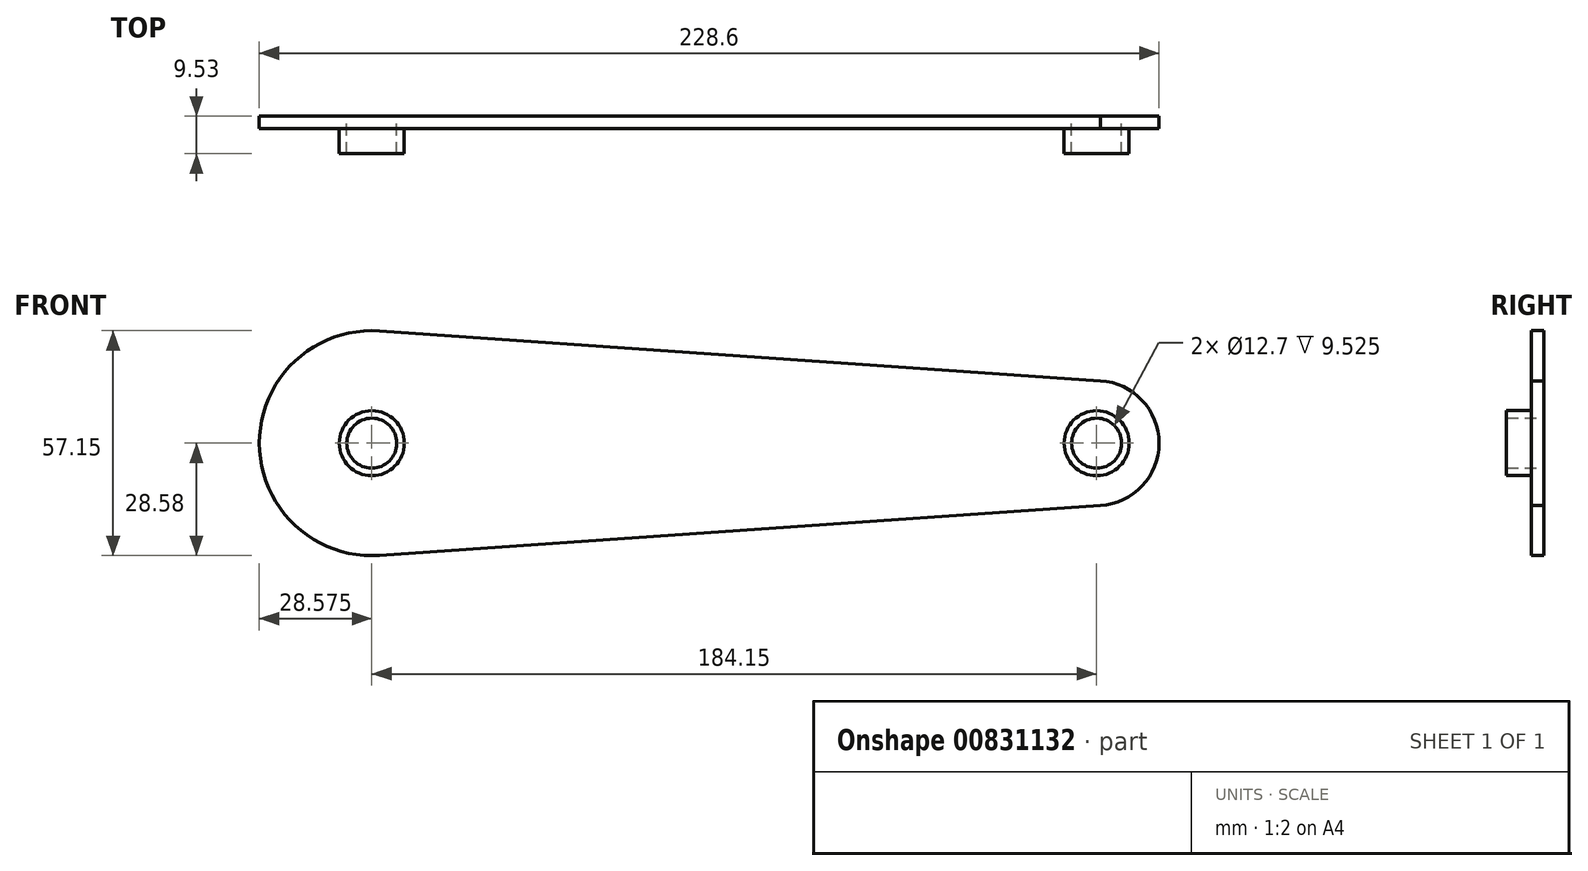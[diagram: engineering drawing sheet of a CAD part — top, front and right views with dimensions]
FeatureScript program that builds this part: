
annotation { "Feature Type Name" : "Feature", "Feature Type Description" : "" }
export const myFeature = defineFeature(function(context is Context, id is Id, definition is map)
    precondition{}
    {
        {
            var Q0;
            Q0=qCreatedBy(makeId("Front.planeOp"),FACE);
            var sketch = newSketch(context, id + "F0", { "sketchPlane" : qUnion([Q0])});
            skArc(sketch, "E0", {"start": v(-90.1, 28.5) * mm, "mid": v(-120.65, 0) * mm, "end": v(-90.1, -28.5) * mm});
            skArc(sketch, "E1", {"start": v(93, -15.85) * mm, "mid": v(107.95, 0) * mm, "end": v(93, 15.85) * mm});
            skCircle(sketch, "E2", {"center": v(-92.08, 0) * mm, "radius": 8.26 * mm});
            skCircle(sketch, "E3", {"center": v(92.08, 0) * mm, "radius": 8.26 * mm});
            skLineSegment(sketch, "E4", {"start": v(93, 15.85) * mm, "end": v(-90.1, 28.5) * mm});
            skLineSegment(sketch, "E5.MirrorCS", {"start": v(93, -15.85) * mm, "end": v(-90.1, -28.5) * mm});
            skSolve(sketch);
        }
        {
            var Q0;
            Q0=makeQuery(id+"F0.imprint","IMPRINT",FACE,{"disambiguationData":[TD([[makeQuery(id+"F0.imprint","IMPRINT",EDGE,{"derivedFrom":sQuery(id+"F0.wireOp",EDGE,"E0")}),1.0]])]});
            extrude(context, id + "F1", {"entities" : qUnion([Q0]), "depth" : 3.17 * mm, "offsetDistance" : 25.4 * mm});
        }
        {
            var Q0;
            Q0=makeQuery(id+"F0.imprint","IMPRINT",FACE,{"disambiguationData":[TD([[makeQuery(id+"F0.imprint","IMPRINT",EDGE,{"derivedFrom":sQuery(id+"F0.wireOp",EDGE,"E2")}),1.0]])]});
            var Q1;
            Q1=makeQuery(id+"F0.imprint","IMPRINT",FACE,{"disambiguationData":[TD([[makeQuery(id+"F0.imprint","IMPRINT",EDGE,{"derivedFrom":sQuery(id+"F0.wireOp",EDGE,"E3")}),1.0]])]});
            extrude(context, id + "F2", {"entities" : qUnion([Q0, Q1]), "operationType" : NewBodyOperationType.ADD, "depth" : 9.52 * mm, "offsetDistance" : 25.4 * mm});
        }
        {
            var Q0;
            Q0=sQuery(id+"F0.wireOp",VERTEX,"E0.center");
            var Q1;
            Q1=sQuery(id+"F0.wireOp",VERTEX,"E1.center");
            var Q2;
            Q2=makeQuery(id+"F1.opExtrude","SWEPT_BODY",BODY,{"disambiguationData":[OSD([sQuery(id+"F0.wireOp",EDGE,"E0"),sQuery(id+"F0.wireOp",EDGE,"E1"),sQuery(id+"F0.wireOp",EDGE,"E2"),sQuery(id+"F0.wireOp",EDGE,"E3"),sQuery(id+"F0.wireOp",EDGE,"E4"),sQuery(id+"F0.wireOp",EDGE,"E5.MirrorCS")])]});
            hole(context, id + "F3", {"style" : HoleStyle.SIMPLE, "endStyle" : HoleEndStyle.THROUGH, "oppositeDirection" : true, "holeDiameter" : 12.7 * mm, "majorDiameter" : 6.35 * mm, "isTappedThrough" : true, "tappedDepth" : 12.7 * mm, "tapClearance" : 3, "locations" : qUnion([Q0, Q1]), "scope" : qUnion([Q2])});
        }
    });
